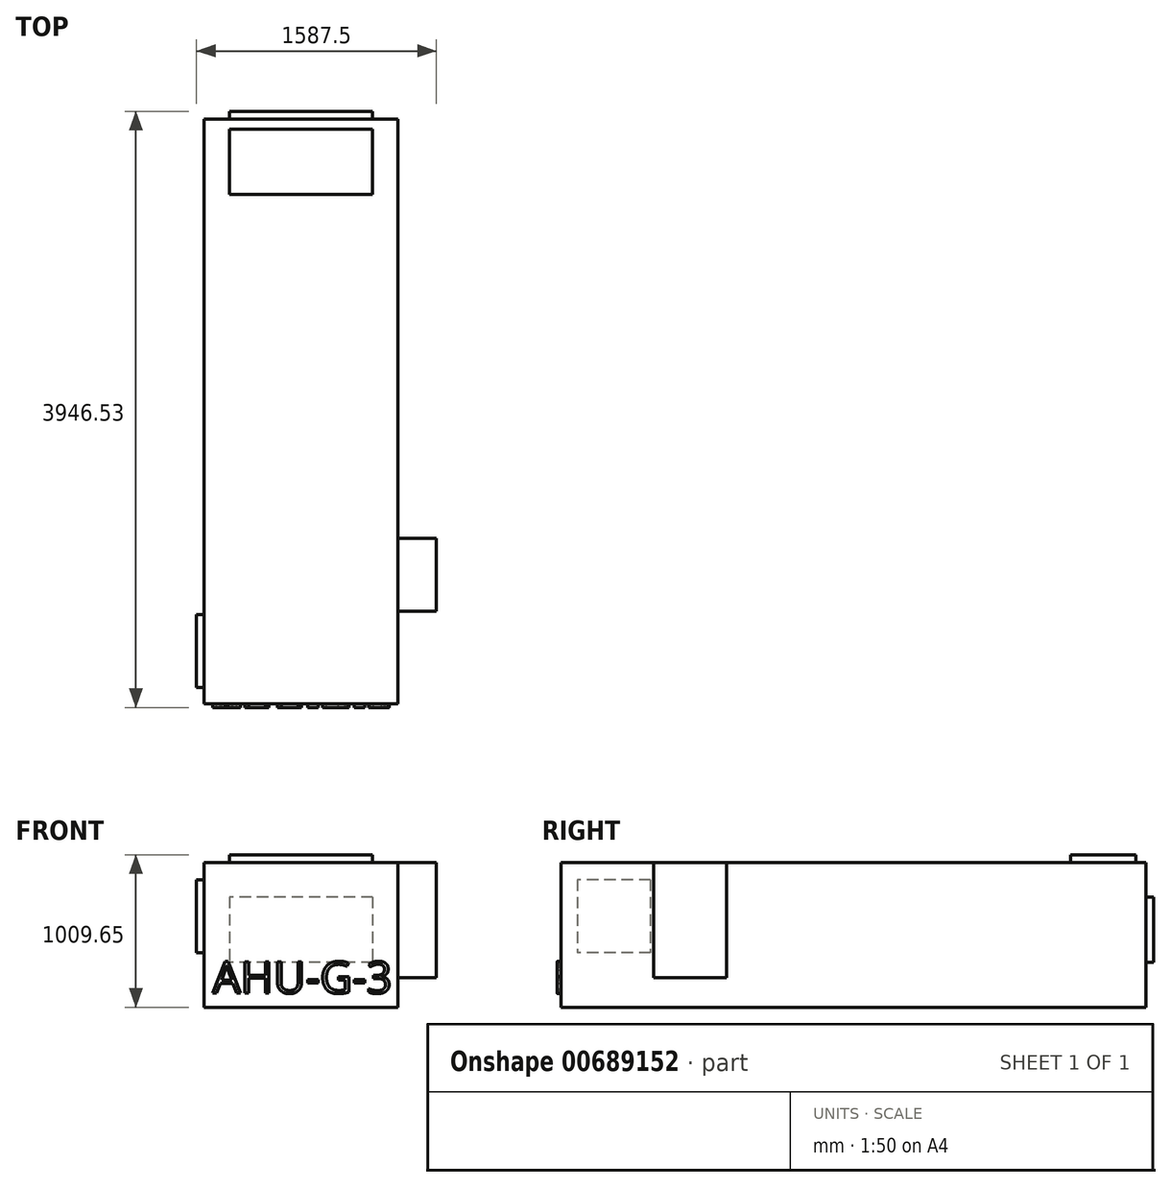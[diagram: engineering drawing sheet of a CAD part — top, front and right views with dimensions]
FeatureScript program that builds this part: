
annotation { "Feature Type Name" : "Feature", "Feature Type Description" : "" }
export const myFeature = defineFeature(function(context is Context, id is Id, definition is map)
    precondition{}
    {
        {
            var Q0;
            Q0=qCreatedBy(makeId("Front.planeOp"),FACE);
            var sketch = newSketch(context, id + "F0", { "sketchPlane" : qUnion([Q0])});
            skLineSegment(sketch, "E0.bottom", {"start": v(-639.94, 406.41) * mm, "end": v(642.76, 406.41) * mm});
            skLineSegment(sketch, "E0.top", {"start": v(-639.94, -552.44) * mm, "end": v(642.76, -552.44) * mm});
            skLineSegment(sketch, "E0.left", {"start": v(-639.94, 406.41) * mm, "end": v(-639.94, -552.44) * mm});
            skLineSegment(sketch, "E0.right", {"start": v(642.76, 406.41) * mm, "end": v(642.76, -552.44) * mm});
            skSolve(sketch);
        }
        {
            var Q0;
            Q0=qSketchRegion(id+"F0",true);
            extrude(context, id + "F1", {"entities" : qUnion([Q0]), "depth" : 3870.32 * mm, "offsetDistance" : 25.4 * mm});
        }
        {
            var Q0;
            Q0=makeQuery(id+"F1.opExtrude","SWEPT_FACE",FACE,{"disambiguationData":[OSD([sQuery(id+"F0.wireOp",EDGE,"E0.left")])]});
            var sketch = newSketch(context, id + "F2", { "sketchPlane" : qUnion([Q0])});
            skLineSegment(sketch, "E1.bottom", {"start": v(3279.78, 292.11) * mm, "end": v(3762.38, 292.11) * mm});
            skLineSegment(sketch, "E1.top", {"start": v(3279.78, -190.49) * mm, "end": v(3762.38, -190.49) * mm});
            skLineSegment(sketch, "E1.left", {"start": v(3279.78, 292.11) * mm, "end": v(3279.78, -190.49) * mm});
            skLineSegment(sketch, "E1.right", {"start": v(3762.38, 292.11) * mm, "end": v(3762.38, -190.49) * mm});
            skSolve(sketch);
        }
        {
            var Q0;
            Q0=makeQuery(id+"F2.imprint","IMPRINT",FACE,{"disambiguationData":[TD([[makeQuery(id+"F2.imprint","IMPRINT",EDGE,{"derivedFrom":sQuery(id+"F2.wireOp",EDGE,"E1.bottom")}),-1.0]])]});
            extrude(context, id + "F3", {"entities" : qUnion([Q0]), "operationType" : NewBodyOperationType.ADD, "depth" : 50.8 * mm, "offsetDistance" : 25.4 * mm});
        }
        {
            var Q0;
            Q0=makeQuery(id+"F1.opExtrude","SWEPT_FACE",FACE,{"disambiguationData":[OSD([sQuery(id+"F0.wireOp",EDGE,"E0.right")])]});
            var sketch = newSketch(context, id + "F4", { "sketchPlane" : qUnion([Q0])});
            skLineSegment(sketch, "E2.bottom", {"start": v(-3257.55, 406.41) * mm, "end": v(-2774.95, 406.41) * mm});
            skLineSegment(sketch, "E2.top", {"start": v(-3257.55, -355.59) * mm, "end": v(-2774.95, -355.59) * mm});
            skLineSegment(sketch, "E2.left", {"start": v(-3257.55, 406.41) * mm, "end": v(-3257.55, -355.59) * mm});
            skLineSegment(sketch, "E2.right", {"start": v(-2774.95, 406.41) * mm, "end": v(-2774.95, -355.59) * mm});
            skSolve(sketch);
        }
        {
            var Q0;
            Q0 = qSketchRegion(id + "F4", true);
            extrude(context, id + "F5", {"entities" : qUnion([Q0]), "depth" : 254 * mm, "offsetDistance" : 25.4 * mm});
        }
        {
            var Q0;
            Q0=makeQuery(id+"F1.opExtrude","CAP_FACE",FACE,{"disambiguationData":[OSD([sQuery(id+"F0.wireOp",EDGE,"E0.bottom"),sQuery(id+"F0.wireOp",EDGE,"E0.top"),sQuery(id+"F0.wireOp",EDGE,"E0.left"),sQuery(id+"F0.wireOp",EDGE,"E0.right")])],"isStart":false});
            var sketch = newSketch(context, id + "F6", { "sketchPlane" : qUnion([Q0])});
            skText(sketch, "E3", { "text": "AHU-G-3", "fontName": "OpenSans-Regular.ttf"});
            const initialGuessF6  = {"E3": [-0.58354, -0.45994, 1, 0, 0.21114]};
            skSetInitialGuess(sketch, initialGuessF6);
            skSolve(sketch);
        }
        {
            var Q0;
            Q0 = qSketchRegion(id + "F6", true);
            extrude(context, id + "F7", {"entities" : qUnion([Q0]), "operationType" : NewBodyOperationType.ADD, "depth" : 25.4 * mm, "offsetDistance" : 25.4 * mm});
        }
        {
            var Q0;
            Q0=makeQuery(id+"F1.opExtrude","SWEPT_FACE",FACE,{"disambiguationData":[OSD([sQuery(id+"F0.wireOp",EDGE,"E0.bottom")])]});
            var sketch = newSketch(context, id + "F8", { "sketchPlane" : qUnion([Q0])});
            skLineSegment(sketch, "E4.bottom", {"start": v(-471.67, -66.68) * mm, "end": v(474.48, -66.68) * mm});
            skLineSegment(sketch, "E4.top", {"start": v(-471.67, -498.48) * mm, "end": v(474.48, -498.47) * mm});
            skLineSegment(sketch, "E4.left", {"start": v(-471.67, -66.68) * mm, "end": v(-471.67, -498.48) * mm});
            skLineSegment(sketch, "E4.right", {"start": v(474.48, -66.67) * mm, "end": v(474.48, -498.47) * mm});
            skSolve(sketch);
        }
        {
            var Q0;
            Q0 = qSketchRegion(id + "F8", true);
            extrude(context, id + "F9", {"entities" : qUnion([Q0]), "operationType" : NewBodyOperationType.ADD, "depth" : 50.8 * mm, "offsetDistance" : 25.4 * mm});
        }
        {
            var Q0;
            Q0=makeQuery(id+"F1.opExtrude","CAP_FACE",FACE,{"disambiguationData":[OSD([sQuery(id+"F0.wireOp",EDGE,"E0.bottom"),sQuery(id+"F0.wireOp",EDGE,"E0.top"),sQuery(id+"F0.wireOp",EDGE,"E0.left"),sQuery(id+"F0.wireOp",EDGE,"E0.right")])],"isStart":true});
            var sketch = newSketch(context, id + "F10", { "sketchPlane" : qUnion([Q0])});
            skLineSegment(sketch, "E5.bottom", {"start": v(-474.48, 177.81) * mm, "end": v(471.67, 177.81) * mm});
            skLineSegment(sketch, "E5.top", {"start": v(-474.48, -253.99) * mm, "end": v(471.67, -253.99) * mm});
            skLineSegment(sketch, "E5.left", {"start": v(-474.48, 177.81) * mm, "end": v(-474.48, -253.99) * mm});
            skLineSegment(sketch, "E5.right", {"start": v(471.67, 177.81) * mm, "end": v(471.67, -253.99) * mm});
            skSolve(sketch);
        }
        {
            var Q0;
            Q0 = qSketchRegion(id + "F10", true);
            extrude(context, id + "F11", {"entities" : qUnion([Q0]), "operationType" : NewBodyOperationType.ADD, "depth" : 50.8 * mm, "offsetDistance" : 25.4 * mm});
        }
    });
